# Revit family: Diverter_Valve-DXV-D35000430
name_source: partatom
category: Pipe Accessories
units: mm (PartAtom-declared; Revit-internal decimal feet)

## family parameters
Always vertical = No
Cut with Voids When Loaded = No
OmniClass Number = 23.65.55.14.11
OmniClass Title = Inlet/Outlet Valves for Liquid Services
Part Type = Normal
Round Connector Dimension = Use Diameter
Shared = Yes
Work Plane-Based = Yes

## types (1)
- D35000430
    Assembly Code = D2090300
    CW Connection = Yes
    Cold Water Connection Diameter = 1/2"
    Cold Water Connection Radius = 1/4"
    Default Elevation = 0"
    Description = 4/3 PORT DIVERTER ROUGH VALVE
    Distance to Lower Finished Wall = 1 5/8"
    Distance to Upper Finished Wall = 2 9/16"
    Finish = Brass-DXV-Cast
    HW Connection = Yes
    Height = 3 1/8"
    Hot Water Connection Diameter = 1"
    Hot Water Connection Radius = 1/4"
    Installation Type = Wall Mounted
    Manufacturer = DXV
    Material = Brass-DXV-Cast
    Model = D35000430
    Price = Prices may vary. Please consult Manufacturer Representative for most up-to-date price list.
    Product Documentation Link = https://dxv01.blob.core.windows.net
    Product Page URL = https://www.dxv.com
    Revised Date = 05/07/2021
    URL = https://www.dxv.com
    Width = 3 1/8"

## geometry (parser evidence)
native form markers: Sweep x2
no freeform markers — native parametric forms only
